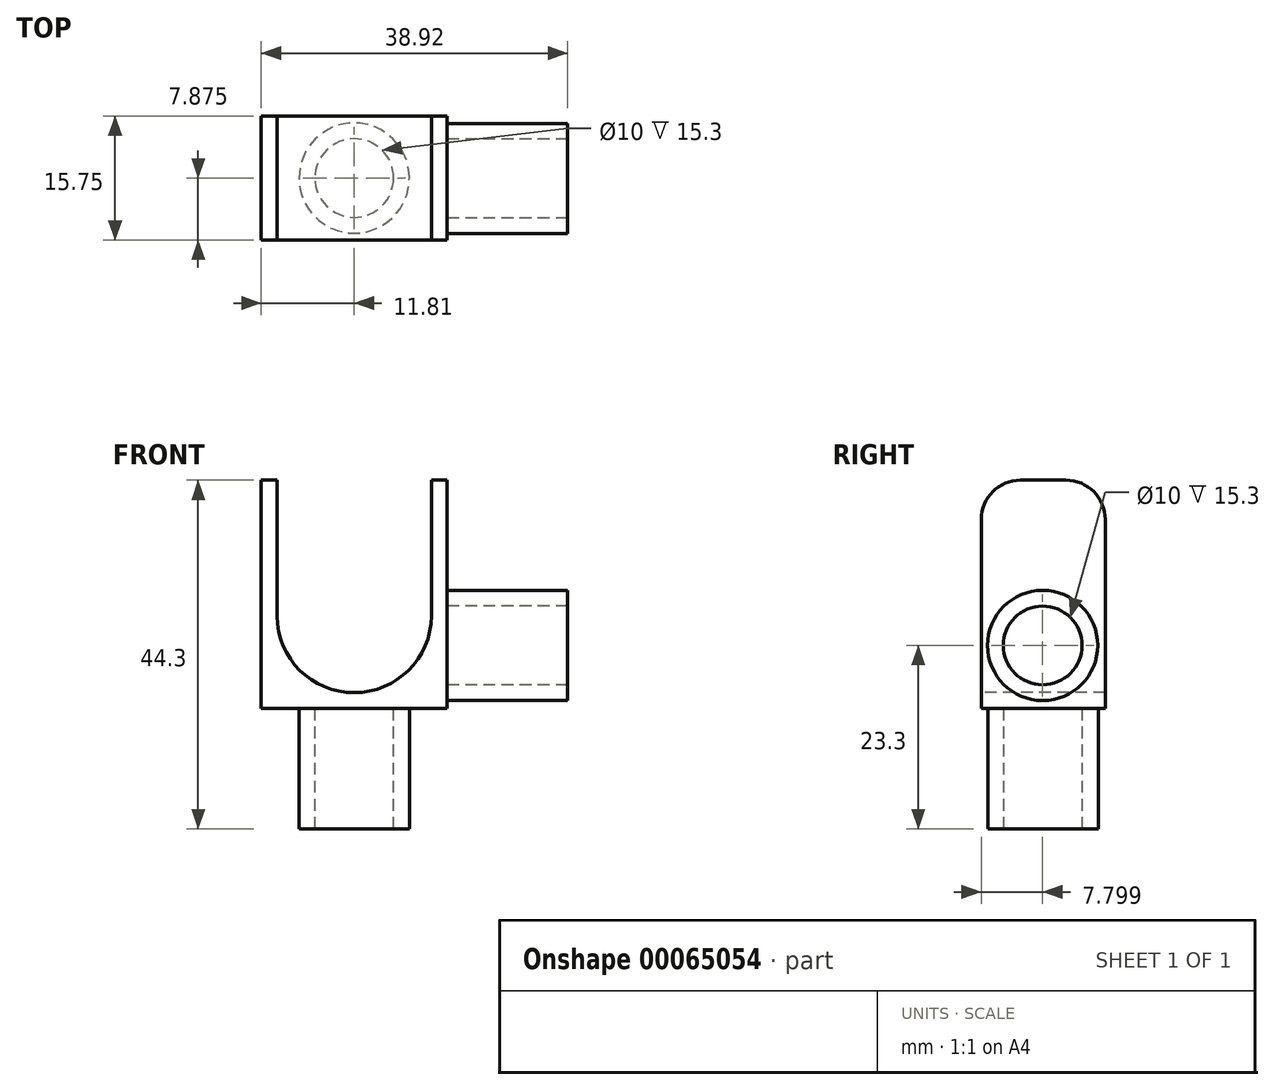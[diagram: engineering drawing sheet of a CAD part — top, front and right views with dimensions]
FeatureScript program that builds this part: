
annotation { "Feature Type Name" : "Feature", "Feature Type Description" : "" }
export const myFeature = defineFeature(function(context is Context, id is Id, definition is map)
    precondition{}
    {
        {
            var Q0;
            Q0=qCreatedBy(makeId("Front.planeOp"),FACE);
            var sketch = newSketch(context, id + "F0", { "sketchPlane" : qUnion([Q0])});
            skLineSegment(sketch, "E0.bottom", {"start": v(-11.8, 22.15) * mm, "end": v(-9.81, 22.15) * mm});
            skLineSegment(sketch, "E0.top", {"start": v(-11.8, -6.85) * mm, "end": v(-9.81, -6.85) * mm});
            skLineSegment(sketch, "E0.left", {"start": v(-11.8, 22.15) * mm, "end": v(-11.8, -6.85) * mm});
            skLineSegment(sketch, "E0.right", {"start": v(-9.81, 22.15) * mm, "end": v(-9.81, -6.85) * mm});
            skLineSegment(sketch, "E1.bottom", {"start": v(-9.81, -6.85) * mm, "end": v(0, -6.85) * mm});
            skLineSegment(sketch, "E1.top", {"start": v(-9.81, -4.85) * mm, "end": v(0, -4.85) * mm});
            skLineSegment(sketch, "E1.left", {"start": v(-9.81, -6.85) * mm, "end": v(-9.81, -4.85) * mm});
            skLineSegment(sketch, "E1.right", {"start": v(0, -6.85) * mm, "end": v(0, -4.85) * mm});
            skLineSegment(sketch, "E2.MirrorCS", {"start": v(9.81, -6.85) * mm, "end": v(9.81, -4.85) * mm});
            skLineSegment(sketch, "E3.MirrorCS", {"start": v(11.8, -6.85) * mm, "end": v(9.81, -6.85) * mm});
            skLineSegment(sketch, "E4.MirrorCS", {"start": v(9.81, -4.85) * mm, "end": v(0, -4.85) * mm});
            skLineSegment(sketch, "E5.MirrorCS", {"start": v(11.8, 22.15) * mm, "end": v(9.81, 22.15) * mm});
            skLineSegment(sketch, "E6.MirrorCS", {"start": v(9.81, -6.85) * mm, "end": v(0, -6.85) * mm});
            skLineSegment(sketch, "E7.MirrorCS", {"start": v(11.8, 22.15) * mm, "end": v(11.8, -6.85) * mm});
            skLineSegment(sketch, "E8.MirrorCS", {"start": v(9.81, 22.15) * mm, "end": v(9.81, -6.85) * mm});
            skSolve(sketch);
        }
        {
            var Q0;
            Q0 = qSketchRegion(id + "F0", true);
            extrude(context, id + "F1", {"entities" : qUnion([Q0]), "depth" : 15.75 * mm});
        }
        {
            var Q0;
            Q0=makeQuery(id+"F1.opExtrude","CAP_EDGE",EDGE,{"disambiguationData":[OSD([sQuery(id+"F0.wireOp",EDGE,"E5.MirrorCS")])],"isStart":false});
            var Q1;
            Q1=makeQuery(id+"F1.opExtrude","CAP_EDGE",EDGE,{"disambiguationData":[OSD([sQuery(id+"F0.wireOp",EDGE,"E0.bottom")])],"isStart":false});
            var Q2;
            Q2=makeQuery(id+"F1.opExtrude","CAP_EDGE",EDGE,{"disambiguationData":[OSD([sQuery(id+"F0.wireOp",EDGE,"E5.MirrorCS")])],"isStart":true});
            var Q3;
            Q3=makeQuery(id+"F1.opExtrude","CAP_EDGE",EDGE,{"disambiguationData":[OSD([sQuery(id+"F0.wireOp",EDGE,"E0.bottom")])],"isStart":true});
            fillet(context, id + "F2", {"entities" : qUnion([Q0, Q1, Q2, Q3]), "radius" : 5 * mm, "tangentPropagation" : true, "allowEdgeOverflow" : false});
        }
        {
            var Q0;
            Q0=makeQuery(id+"F1.opExtrude","SWEPT_FACE",FACE,{"disambiguationData":[OSD([sQuery(id+"F0.wireOp",EDGE,"E7.MirrorCS")])]});
            var sketch = newSketch(context, id + "F3", { "sketchPlane" : qUnion([Q0])});
            skCircle(sketch, "E9", {"center": v(-7.95, 1.15) * mm, "radius": 7 * mm});
            skPoint(sketch, "E9.first.point", {"position": v(-7.88, -6.85) * mm});
            skPoint(sketch, "E9.second.point", {"position": v(0, 1.08) * mm});
            skPoint(sketch, "E9.third.point", {"position": v(-15.75, 0) * mm});
            skCircle(sketch, "E10", {"center": v(-7.95, 1.15) * mm, "radius": 5 * mm});
            skSolve(sketch);
        }
        {
            var Q0;
            Q0 = qSketchRegion(id + "F3", true);
            extrude(context, id + "F4", {"entities" : qUnion([Q0]), "operationType" : NewBodyOperationType.ADD, "depth" : 15.3 * mm});
        }
        {
            var Q0;
            Q0=makeQuery(id+"F1.opExtrude","SWEPT_FACE",FACE,{"disambiguationData":[OSD([sQuery(id+"F0.wireOp",EDGE,"E0.top"),sQuery(id+"F0.wireOp",EDGE,"E1.bottom"),sQuery(id+"F0.wireOp",EDGE,"E3.MirrorCS"),sQuery(id+"F0.wireOp",EDGE,"E6.MirrorCS")])]});
            var sketch = newSketch(context, id + "F5", { "sketchPlane" : qUnion([Q0])});
            skCircle(sketch, "E11", {"center": v(0, 7.88) * mm, "radius": 7 * mm});
            skPoint(sketch, "E11.first.point", {"position": v(0, 15.75) * mm});
            skPoint(sketch, "E11.second.point", {"position": v(-6.79, 7.3) * mm});
            skPoint(sketch, "E11.third.point", {"position": v(0, 0) * mm});
            skCircle(sketch, "E12", {"center": v(0, 7.88) * mm, "radius": 5 * mm});
            skPoint(sketch, "E13", {"position": v(-11.8, 7.88) * mm});
            skSolve(sketch);
        }
        {
            var Q0;
            Q0 = qSketchRegion(id + "F5", true);
            extrude(context, id + "F6", {"entities" : qUnion([Q0]), "operationType" : NewBodyOperationType.ADD, "depth" : 15.3 * mm});
        }
        {
            var Q0;
            Q0=makeQuery(id+"F1.opExtrude","CAP_FACE",FACE,{"disambiguationData":[OSD([sQuery(id+"F0.wireOp",EDGE,"E0.bottom"),sQuery(id+"F0.wireOp",EDGE,"E0.top"),sQuery(id+"F0.wireOp",EDGE,"E0.left"),sQuery(id+"F0.wireOp",EDGE,"E0.right"),sQuery(id+"F0.wireOp",EDGE,"E1.bottom"),sQuery(id+"F0.wireOp",EDGE,"E1.top"),sQuery(id+"F0.wireOp",EDGE,"E3.MirrorCS"),sQuery(id+"F0.wireOp",EDGE,"E4.MirrorCS"),sQuery(id+"F0.wireOp",EDGE,"E5.MirrorCS"),sQuery(id+"F0.wireOp",EDGE,"E6.MirrorCS"),sQuery(id+"F0.wireOp",EDGE,"E7.MirrorCS"),sQuery(id+"F0.wireOp",EDGE,"E8.MirrorCS")])],"isStart":false});
            var sketch = newSketch(context, id + "F7", { "sketchPlane" : qUnion([Q0])});
            skLineSegment(sketch, "E14", {"start": v(9.81, 5.04) * mm, "end": v(9.81, -4.85) * mm});
            skLineSegment(sketch, "E15", {"start": v(9.81, -4.85) * mm, "end": v(-9.81, -4.85) * mm});
            skLineSegment(sketch, "E16", {"start": v(-9.81, -4.85) * mm, "end": v(-9.81, 5.04) * mm});
            skArc(sketch, "E17", {"start": v(-9.81, 5.04) * mm, "mid": v(0, -4.85) * mm, "end": v(9.81, 5.04) * mm});
            skPoint(sketch, "E18", {"position": v(9.81, 6.15) * mm});
            skSolve(sketch);
        }
        {
            var Q0;
            Q0 = qSketchRegion(id + "F7", true);
            var Q1;
            Q1=makeQuery(id+"F1.opExtrude","CAP_FACE",FACE,{"disambiguationData":[OSD([sQuery(id+"F0.wireOp",EDGE,"E0.bottom"),sQuery(id+"F0.wireOp",EDGE,"E0.top"),sQuery(id+"F0.wireOp",EDGE,"E0.left"),sQuery(id+"F0.wireOp",EDGE,"E0.right"),sQuery(id+"F0.wireOp",EDGE,"E1.bottom"),sQuery(id+"F0.wireOp",EDGE,"E1.top"),sQuery(id+"F0.wireOp",EDGE,"E3.MirrorCS"),sQuery(id+"F0.wireOp",EDGE,"E4.MirrorCS"),sQuery(id+"F0.wireOp",EDGE,"E5.MirrorCS"),sQuery(id+"F0.wireOp",EDGE,"E6.MirrorCS"),sQuery(id+"F0.wireOp",EDGE,"E7.MirrorCS"),sQuery(id+"F0.wireOp",EDGE,"E8.MirrorCS")])],"isStart":true});
            extrude(context, id + "F8", {"entities" : qUnion([Q0]), "operationType" : NewBodyOperationType.ADD, "endBound" : BoundingType.UP_TO_SURFACE, "oppositeDirection" : true, "endBoundEntityFace" : qUnion([Q1]), "depth" : 25 * mm});
        }
    });
